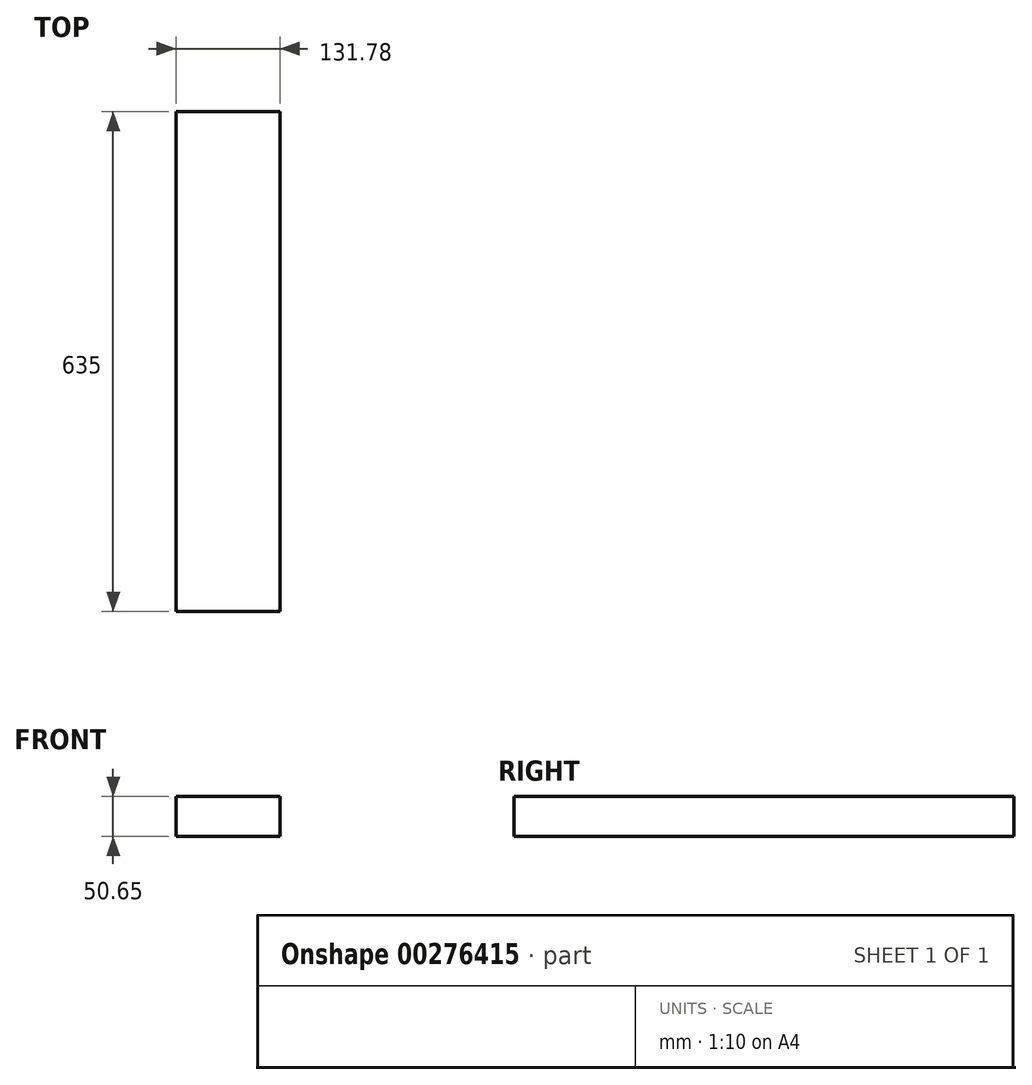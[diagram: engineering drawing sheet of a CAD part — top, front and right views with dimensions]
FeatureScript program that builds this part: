
annotation { "Feature Type Name" : "Feature", "Feature Type Description" : "" }
export const myFeature = defineFeature(function(context is Context, id is Id, definition is map)
    precondition{}
    {
        {
            var Q0;
            Q0=qCreatedBy(makeId("Front.planeOp"),FACE);
            var sketch = newSketch(context, id + "F0", { "sketchPlane" : qUnion([Q0])});
            skLineSegment(sketch, "E0.bottom", {"start": v(-113.4, 79.11) * mm, "end": v(18.38, 79.11) * mm});
            skLineSegment(sketch, "E0.top", {"start": v(-113.4, 28.46) * mm, "end": v(18.38, 28.46) * mm});
            skLineSegment(sketch, "E0.left", {"start": v(-113.4, 79.11) * mm, "end": v(-113.4, 28.46) * mm});
            skLineSegment(sketch, "E0.right", {"start": v(18.38, 79.11) * mm, "end": v(18.38, 28.46) * mm});
            skSolve(sketch);
        }
        {
            var Q0;
            Q0 = qSketchRegion(id + "F0", true);
            extrude(context, id + "F1", {"entities" : qUnion([Q0]), "depth" : 635 * mm});
        }
    });
